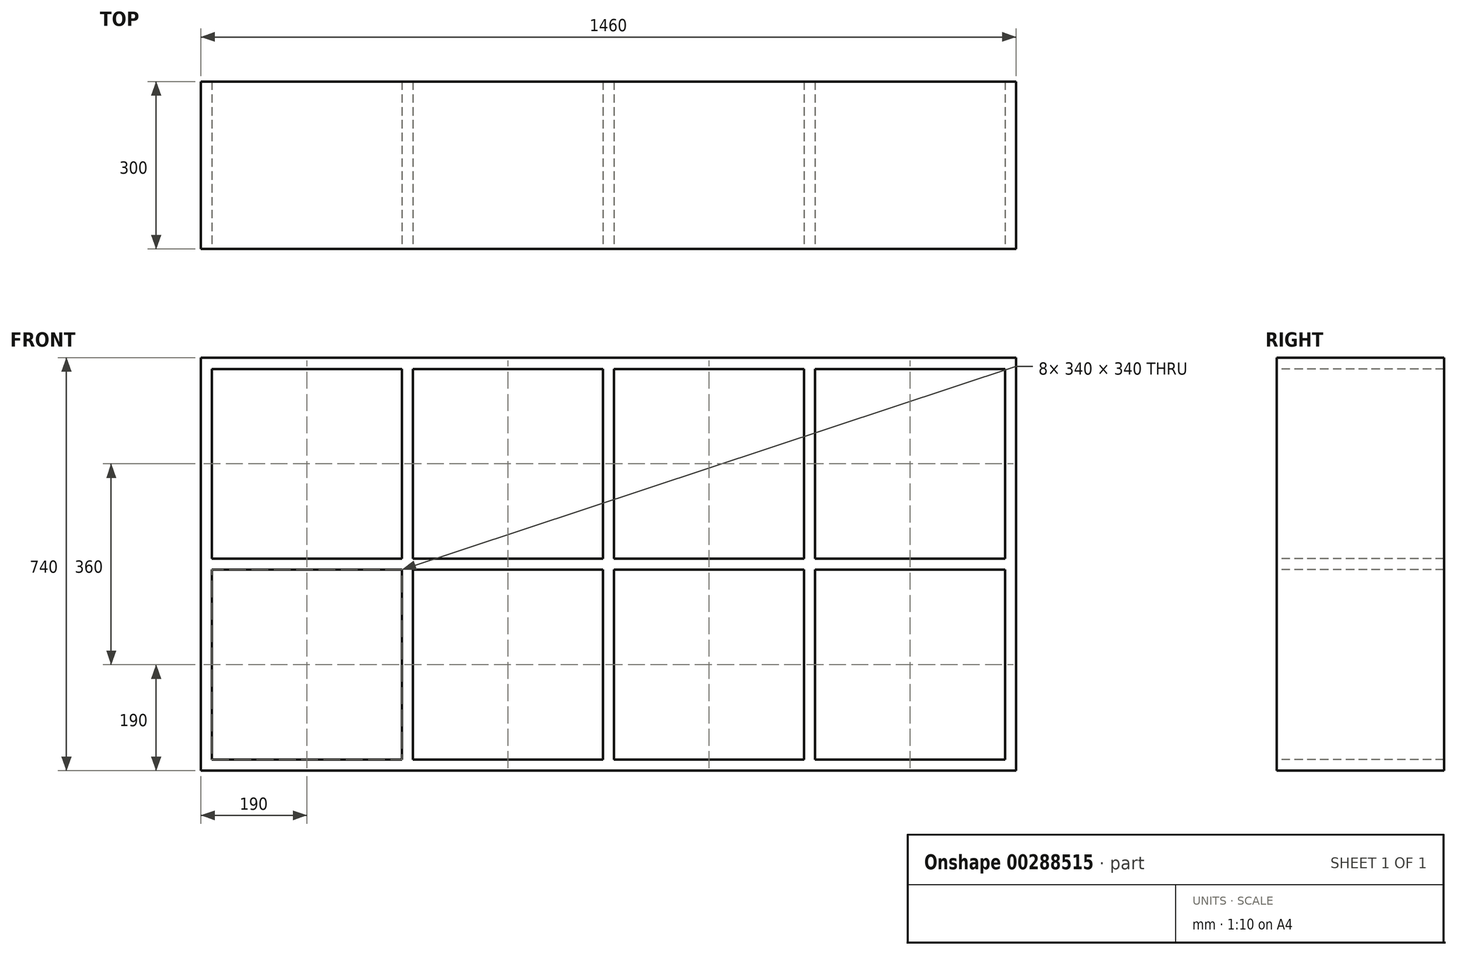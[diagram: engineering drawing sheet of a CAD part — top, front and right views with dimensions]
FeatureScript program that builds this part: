
annotation { "Feature Type Name" : "Feature", "Feature Type Description" : "" }
export const myFeature = defineFeature(function(context is Context, id is Id, definition is map)
    precondition{}
    {
        {
            var Q0;
            Q0=qCreatedBy(makeId("Front.planeOp"),FACE);
            var sketch = newSketch(context, id + "F0", { "sketchPlane" : qUnion([Q0])});
            skLineSegment(sketch, "E0.bottom", {"start": v(0, 0) * mm, "end": v(1460, 0) * mm});
            skLineSegment(sketch, "E0.top", {"start": v(0, 740) * mm, "end": v(1460, 740) * mm});
            skLineSegment(sketch, "E0.left", {"start": v(0, 0) * mm, "end": v(0, 740) * mm});
            skLineSegment(sketch, "E0.right", {"start": v(1460, 0) * mm, "end": v(1460, 740) * mm});
            skSolve(sketch);
        }
        {
            var Q0;
            Q0 = qSketchRegion(id + "F0", true);
            extrude(context, id + "F1", {"entities" : qUnion([Q0]), "depth" : 300 * mm});
        }
        {
            var Q0;
            Q0=makeQuery(id+"F1.opExtrude","CAP_FACE",FACE,{"disambiguationData":[OSD([sQuery(id+"F0.wireOp",EDGE,"E0.bottom"),sQuery(id+"F0.wireOp",EDGE,"E0.top"),sQuery(id+"F0.wireOp",EDGE,"E0.left"),sQuery(id+"F0.wireOp",EDGE,"E0.right")])],"isStart":false});
            var sketch = newSketch(context, id + "F2", { "sketchPlane" : qUnion([Q0])});
            skLineSegment(sketch, "E1.bottom", {"start": v(20, 20) * mm, "end": v(360, 20) * mm});
            skLineSegment(sketch, "E1.top", {"start": v(20, 360) * mm, "end": v(360, 360) * mm});
            skLineSegment(sketch, "E1.left", {"start": v(20, 20) * mm, "end": v(20, 360) * mm});
            skLineSegment(sketch, "E1.right", {"start": v(360, 20) * mm, "end": v(360, 360) * mm});
            skLineSegment(sketch, "E2.0.1.0", {"start": v(360, 380) * mm, "end": v(360, 720) * mm});
            skLineSegment(sketch, "E2.0.1.1", {"start": v(20, 380) * mm, "end": v(20, 720) * mm});
            skLineSegment(sketch, "E2.0.1.2", {"start": v(20, 720) * mm, "end": v(360, 720) * mm});
            skLineSegment(sketch, "E2.0.1.3", {"start": v(20, 380) * mm, "end": v(360, 380) * mm});
            skLineSegment(sketch, "E2.1.0.0", {"start": v(720, 20) * mm, "end": v(720, 360) * mm});
            skLineSegment(sketch, "E2.1.0.1", {"start": v(380, 20) * mm, "end": v(380, 360) * mm});
            skLineSegment(sketch, "E2.1.0.2", {"start": v(380, 360) * mm, "end": v(720, 360) * mm});
            skLineSegment(sketch, "E2.1.0.3", {"start": v(380, 20) * mm, "end": v(720, 20) * mm});
            skLineSegment(sketch, "E2.1.1.0", {"start": v(720, 380) * mm, "end": v(720, 720) * mm});
            skLineSegment(sketch, "E2.1.1.1", {"start": v(380, 380) * mm, "end": v(380, 720) * mm});
            skLineSegment(sketch, "E2.1.1.2", {"start": v(380, 720) * mm, "end": v(720, 720) * mm});
            skLineSegment(sketch, "E2.1.1.3", {"start": v(380, 380) * mm, "end": v(720, 380) * mm});
            skLineSegment(sketch, "E2.2.0.0", {"start": v(1080, 20) * mm, "end": v(1080, 360) * mm});
            skLineSegment(sketch, "E2.2.0.1", {"start": v(740, 20) * mm, "end": v(740, 360) * mm});
            skLineSegment(sketch, "E2.2.0.2", {"start": v(740, 360) * mm, "end": v(1080, 360) * mm});
            skLineSegment(sketch, "E2.2.0.3", {"start": v(740, 20) * mm, "end": v(1080, 20) * mm});
            skLineSegment(sketch, "E2.2.1.0", {"start": v(1080, 380) * mm, "end": v(1080, 720) * mm});
            skLineSegment(sketch, "E2.2.1.1", {"start": v(740, 380) * mm, "end": v(740, 720) * mm});
            skLineSegment(sketch, "E2.2.1.2", {"start": v(740, 720) * mm, "end": v(1080, 720) * mm});
            skLineSegment(sketch, "E2.2.1.3", {"start": v(740, 380) * mm, "end": v(1080, 380) * mm});
            skLineSegment(sketch, "E2.3.0.0", {"start": v(1440, 20) * mm, "end": v(1440, 360) * mm});
            skLineSegment(sketch, "E2.3.0.1", {"start": v(1100, 20) * mm, "end": v(1100, 360) * mm});
            skLineSegment(sketch, "E2.3.0.2", {"start": v(1100, 360) * mm, "end": v(1440, 360) * mm});
            skLineSegment(sketch, "E2.3.0.3", {"start": v(1100, 20) * mm, "end": v(1440, 20) * mm});
            skLineSegment(sketch, "E2.3.1.0", {"start": v(1440, 380) * mm, "end": v(1440, 720) * mm});
            skLineSegment(sketch, "E2.3.1.1", {"start": v(1100, 380) * mm, "end": v(1100, 720) * mm});
            skLineSegment(sketch, "E2.3.1.2", {"start": v(1100, 720) * mm, "end": v(1440, 720) * mm});
            skLineSegment(sketch, "E2.3.1.3", {"start": v(1100, 380) * mm, "end": v(1440, 380) * mm});
            skLineSegment(sketch, "E2.direction1", {"start": v(20, 20) * mm, "end": v(380, 20) * mm, "construction": true});
            skLineSegment(sketch, "E2.direction2", {"start": v(20, 20) * mm, "end": v(20, 380) * mm, "construction": true});
            skSolve(sketch);
        }
        {
            var Q0;
            Q0 = qSketchRegion(id + "F2", true);
            extrude(context, id + "F3", {"entities" : qUnion([Q0]), "operationType" : NewBodyOperationType.REMOVE, "endBound" : BoundingType.UP_TO_NEXT, "oppositeDirection" : true, "depth" : 25 * mm});
        }
    });
